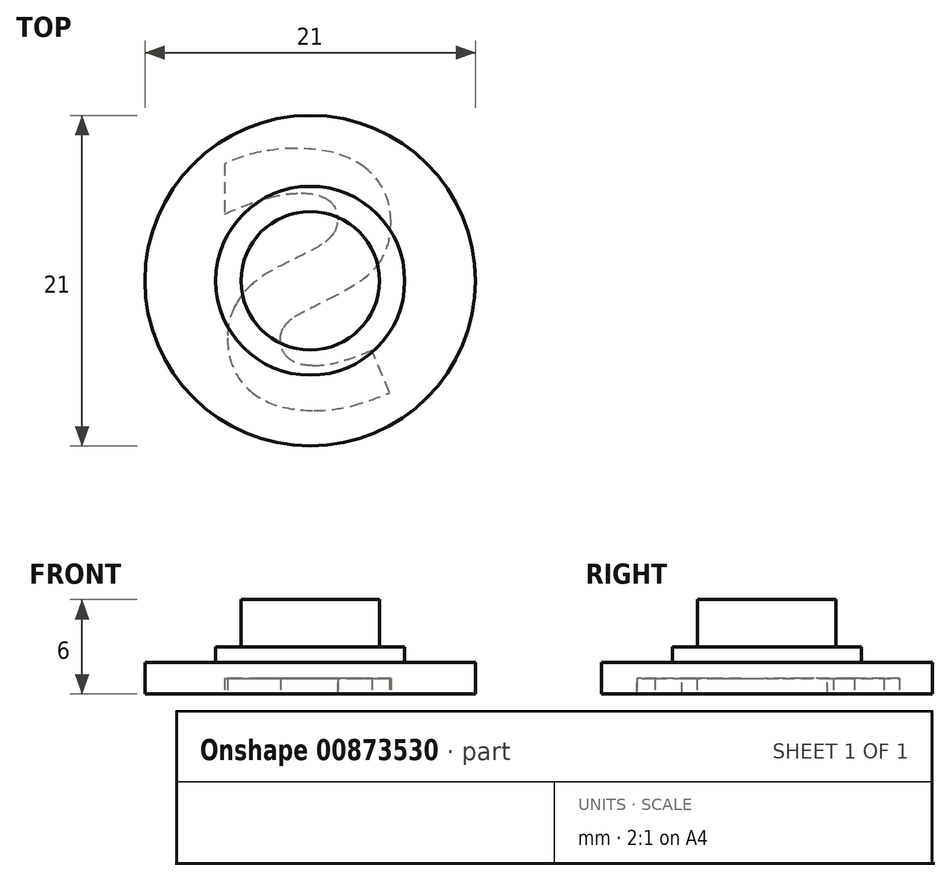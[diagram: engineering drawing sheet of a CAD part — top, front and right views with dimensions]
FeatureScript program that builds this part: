
annotation { "Feature Type Name" : "Feature", "Feature Type Description" : "" }
export const myFeature = defineFeature(function(context is Context, id is Id, definition is map)
    precondition{}
    {
        {
            var Q0;
            Q0=qCreatedBy(makeId("Top.planeOp"),FACE);
            var sketch = newSketch(context, id + "F0", { "sketchPlane" : qUnion([Q0])});
            skCircle(sketch, "E0", {"center": v(0, 0) * mm, "radius": 10.5 * mm});
            skSolve(sketch);
        }
        {
            var Q0;
            Q0 = qSketchRegion(id + "F0", true);
            extrude(context, id + "F1", {"entities" : qUnion([Q0]), "depth" : 2 * mm, "offsetDistance" : 25 * mm});
        }
        {
            var Q0;
            Q0=makeQuery(id+"F1.opExtrude","CAP_FACE",FACE,{"disambiguationData":[OSD([sQuery(id+"F0.wireOp",EDGE,"E0")])],"isStart":false});
            var sketch = newSketch(context, id + "F2", { "sketchPlane" : qUnion([Q0])});
            skCircle(sketch, "E1", {"center": v(0, 0) * mm, "radius": 6 * mm});
            skSolve(sketch);
        }
        {
            var Q0;
            Q0 = qSketchRegion(id + "F2", true);
            extrude(context, id + "F3", {"entities" : qUnion([Q0]), "operationType" : NewBodyOperationType.ADD, "depth" : 1 * mm, "offsetDistance" : 25 * mm});
        }
        {
            var Q0;
            Q0=makeQuery(id+"F3.opExtrude","CAP_FACE",FACE,{"disambiguationData":[OSD([sQuery(id+"F2.wireOp",EDGE,"E1")])],"isStart":false});
            var sketch = newSketch(context, id + "F4", { "sketchPlane" : qUnion([Q0])});
            skCircle(sketch, "E2", {"center": v(0, 0) * mm, "radius": 4.4 * mm});
            skSolve(sketch);
        }
        {
            var Q0;
            Q0 = qSketchRegion(id + "F4", true);
            extrude(context, id + "F5", {"entities" : qUnion([Q0]), "operationType" : NewBodyOperationType.ADD, "depth" : 3 * mm, "offsetDistance" : 25 * mm});
        }
        {
            var Q0;
            Q0=makeQuery(id+"F1.opExtrude","CAP_FACE",FACE,{"disambiguationData":[OSD([sQuery(id+"F0.wireOp",EDGE,"E0")])],"isStart":true});
            var sketch = newSketch(context, id + "F6", { "sketchPlane" : qUnion([Q0])});
            skText(sketch, "E3", { "text": "S", "fontName": "OpenSans-Bold.ttf"});
            const initialGuessF6  = {"E3": [-0.00648, -0.00818, 1, 0, 0.01633]};
            skSetInitialGuess(sketch, initialGuessF6);
            skSolve(sketch);
        }
        {
            var Q0;
            Q0 = qSketchRegion(id + "F6", true);
            extrude(context, id + "F7", {"entities" : qUnion([Q0]), "operationType" : NewBodyOperationType.REMOVE, "oppositeDirection" : true, "depth" : 1 * mm, "offsetDistance" : 25 * mm});
        }
    });
